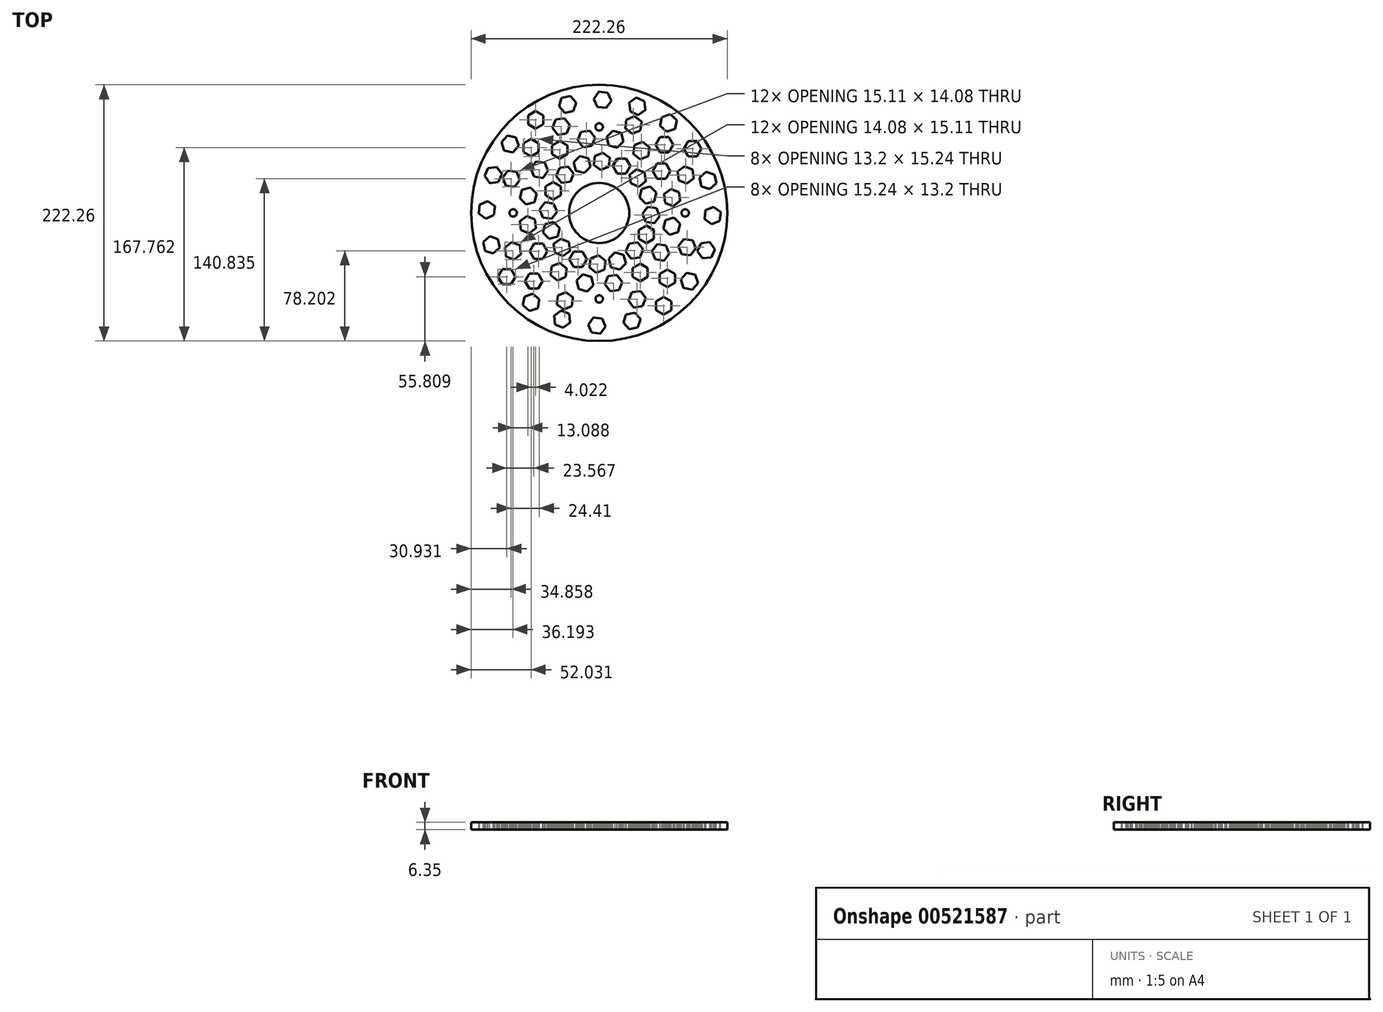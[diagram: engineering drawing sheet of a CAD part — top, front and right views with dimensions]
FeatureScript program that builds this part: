
annotation { "Feature Type Name" : "Feature", "Feature Type Description" : "" }
export const myFeature = defineFeature(function(context is Context, id is Id, definition is map)
    precondition{}
    {
        {
            var Q0;
            Q0=qCreatedBy(makeId("Top.planeOp"),FACE);
            var sketch = newSketch(context, id + "F0", { "sketchPlane" : qUnion([Q0])});
            skCircle(sketch, "E0", {"center": v(0, 0) * mm, "radius": 111.13 * mm});
            skSolve(sketch);
        }
        {
            var Q0;
            Q0=makeQuery(id+"F0.imprint","IMPRINT",FACE,{"disambiguationData":[TD([[makeQuery(id+"F0.imprint","IMPRINT",EDGE,{"derivedFrom":sQuery(id+"F0.wireOp",EDGE,"E0")}),1.0]])]});
            extrude(context, id + "F1", {"entities" : qUnion([Q0]), "depth" : 6.35 * mm, "offsetDistance" : 25.4 * mm});
        }
        {
            var Q0;
            Q0=makeQuery(id+"F1.opExtrude","CAP_FACE",FACE,{"disambiguationData":[OSD([sQuery(id+"F0.wireOp",EDGE,"E0")])],"isStart":false});
            var sketch = newSketch(context, id + "F2", { "sketchPlane" : qUnion([Q0])});
            skCircle(sketch, "E1", {"center": v(0, 0) * mm, "radius": 74.61 * mm, "construction": true});
            skPoint(sketch, "E2", {"position": v(-74.61, 0) * mm});
            skPoint(sketch, "E3", {"position": v(0, -74.61) * mm});
            skPoint(sketch, "E4", {"position": v(74.61, 0) * mm});
            skPoint(sketch, "E5", {"position": v(0, 74.61) * mm});
            skSolve(sketch);
        }
        {
            var Q0;
            Q0=sQuery(id+"F2.wireOp",VERTEX,"E5");
            var Q1;
            Q1=sQuery(id+"F2.wireOp",VERTEX,"E4");
            var Q2;
            Q2=sQuery(id+"F2.wireOp",VERTEX,"E3");
            var Q3;
            Q3=sQuery(id+"F2.wireOp",VERTEX,"E2");
            var Q4;
            Q4=makeQuery(id+"F1.opExtrude","SWEPT_BODY",BODY,{"disambiguationData":[OSD([sQuery(id+"F0.wireOp",EDGE,"E0")])]});
            hole(context, id + "F3", {"style" : HoleStyle.SIMPLE, "endStyle" : HoleEndStyle.THROUGH, "holeDiameter" : 6.35 * mm, "majorDiameter" : 6.35 * mm, "tappedDepth" : 25.4 * mm, "tapClearance" : 3, "locations" : qUnion([Q0, Q1, Q2, Q3]), "scope" : qUnion([Q4])});
        }
        {
            var Q0;
            Q0=makeQuery(id+"F1.opExtrude","CAP_FACE",FACE,{"disambiguationData":[OSD([sQuery(id+"F0.wireOp",EDGE,"E0")])],"isStart":false});
            var sketch = newSketch(context, id + "F4", { "sketchPlane" : qUnion([Q0])});
            skCircle(sketch, "E6.cCircle", {"center": v(-55.08, 80.89) * mm, "radius": 6.6 * mm, "construction": true});
            skLineSegment(sketch, "E6.0", {"start": v(-48.48, 84.7) * mm, "end": v(-48.48, 77.08) * mm});
            skLineSegment(sketch, "E6.1", {"start": v(-48.48, 77.08) * mm, "end": v(-55.08, 73.27) * mm});
            skLineSegment(sketch, "E6.2", {"start": v(-55.08, 73.27) * mm, "end": v(-61.68, 77.08) * mm});
            skLineSegment(sketch, "E6.3", {"start": v(-61.68, 77.08) * mm, "end": v(-61.68, 84.7) * mm});
            skLineSegment(sketch, "E6.4", {"start": v(-61.68, 84.7) * mm, "end": v(-55.08, 88.5) * mm});
            skLineSegment(sketch, "E6.5", {"start": v(-55.08, 88.5) * mm, "end": v(-48.48, 84.7) * mm});
            skPoint(sketch, "E6.0.midPoint", {"position": v(-48.48, 80.89) * mm});
            skCircle(sketch, "E7", {"center": v(0, 0) * mm, "radius": 97.86 * mm, "construction": true});
            skLineSegment(sketch, "E8.1.0", {"start": v(-74.93, 52.53) * mm, "end": v(-82.38, 54.11) * mm});
            skLineSegment(sketch, "E8.1.1", {"start": v(-72.19, 65.44) * mm, "end": v(-69.83, 58.2) * mm});
            skLineSegment(sketch, "E8.1.2", {"start": v(-79.64, 67.02) * mm, "end": v(-72.19, 65.44) * mm});
            skLineSegment(sketch, "E8.1.3", {"start": v(-84.74, 61.36) * mm, "end": v(-79.64, 67.02) * mm});
            skLineSegment(sketch, "E8.1.4", {"start": v(-82.38, 54.11) * mm, "end": v(-84.74, 61.36) * mm});
            skCircle(sketch, "E8.1.5", {"center": v(-77.29, 59.78) * mm, "radius": 6.6 * mm, "construction": true});
            skLineSegment(sketch, "E8.1.6", {"start": v(-69.83, 58.2) * mm, "end": v(-74.93, 52.53) * mm});
            skPoint(sketch, "E8.1.7", {"position": v(-71, 61.82) * mm});
            skLineSegment(sketch, "E8.2.0", {"start": v(-87.4, 26.67) * mm, "end": v(-94.98, 25.87) * mm});
            skLineSegment(sketch, "E8.2.1", {"start": v(-88.78, 39.8) * mm, "end": v(-84.3, 33.63) * mm});
            skLineSegment(sketch, "E8.2.2", {"start": v(-96.36, 39) * mm, "end": v(-88.78, 39.8) * mm});
            skLineSegment(sketch, "E8.2.3", {"start": v(-99.46, 32.04) * mm, "end": v(-96.36, 39) * mm});
            skLineSegment(sketch, "E8.2.4", {"start": v(-94.98, 25.87) * mm, "end": v(-99.46, 32.04) * mm});
            skCircle(sketch, "E8.2.5", {"center": v(-91.88, 32.84) * mm, "radius": 6.6 * mm, "construction": true});
            skLineSegment(sketch, "E8.2.6", {"start": v(-84.3, 33.63) * mm, "end": v(-87.4, 26.67) * mm});
            skPoint(sketch, "E8.2.7", {"position": v(-86.54, 36.71) * mm});
            skLineSegment(sketch, "E8.3.0", {"start": v(-91.28, -1.78) * mm, "end": v(-98.24, -4.88) * mm});
            skLineSegment(sketch, "E8.3.1", {"start": v(-96.64, 10.28) * mm, "end": v(-90.48, 5.8) * mm});
            skLineSegment(sketch, "E8.3.2", {"start": v(-103.6, 7.18) * mm, "end": v(-96.64, 10.28) * mm});
            skLineSegment(sketch, "E8.3.3", {"start": v(-104.4, -0.4) * mm, "end": v(-103.6, 7.18) * mm});
            skLineSegment(sketch, "E8.3.4", {"start": v(-98.24, -4.88) * mm, "end": v(-104.4, -0.4) * mm});
            skCircle(sketch, "E8.3.5", {"center": v(-97.44, 2.7) * mm, "radius": 6.6 * mm, "construction": true});
            skLineSegment(sketch, "E8.3.6", {"start": v(-90.48, 5.8) * mm, "end": v(-91.28, -1.78) * mm});
            skPoint(sketch, "E8.3.7", {"position": v(-93.56, 8.04) * mm});
            skLineSegment(sketch, "E8.4.0", {"start": v(-86.17, -30.03) * mm, "end": v(-91.83, -35.13) * mm});
            skLineSegment(sketch, "E8.4.1", {"start": v(-95, -20.22) * mm, "end": v(-87.75, -22.58) * mm});
            skLineSegment(sketch, "E8.4.2", {"start": v(-100.66, -25.32) * mm, "end": v(-95, -20.22) * mm});
            skLineSegment(sketch, "E8.4.3", {"start": v(-99.08, -32.77) * mm, "end": v(-100.66, -25.32) * mm});
            skLineSegment(sketch, "E8.4.4", {"start": v(-91.83, -35.13) * mm, "end": v(-99.08, -32.77) * mm});
            skCircle(sketch, "E8.4.5", {"center": v(-93.42, -27.68) * mm, "radius": 6.6 * mm, "construction": true});
            skLineSegment(sketch, "E8.4.6", {"start": v(-87.75, -22.58) * mm, "end": v(-86.17, -30.03) * mm});
            skPoint(sketch, "E8.4.7", {"position": v(-91.38, -21.4) * mm});
            skLineSegment(sketch, "E8.5.0", {"start": v(-72.58, -55.32) * mm, "end": v(-76.39, -61.92) * mm});
            skLineSegment(sketch, "E8.5.1", {"start": v(-84, -48.72) * mm, "end": v(-76.39, -48.72) * mm});
            skLineSegment(sketch, "E8.5.2", {"start": v(-87.82, -55.32) * mm, "end": v(-84, -48.72) * mm});
            skLineSegment(sketch, "E8.5.3", {"start": v(-84, -61.92) * mm, "end": v(-87.82, -55.32) * mm});
            skLineSegment(sketch, "E8.5.4", {"start": v(-76.39, -61.92) * mm, "end": v(-84, -61.92) * mm});
            skCircle(sketch, "E8.5.5", {"center": v(-80.2, -55.32) * mm, "radius": 6.6 * mm, "construction": true});
            skLineSegment(sketch, "E8.5.6", {"start": v(-76.39, -48.72) * mm, "end": v(-72.58, -55.32) * mm});
            skPoint(sketch, "E8.5.7", {"position": v(-80.2, -48.72) * mm});
            skLineSegment(sketch, "E8.6.0", {"start": v(-51.84, -75.18) * mm, "end": v(-53.42, -82.63) * mm});
            skLineSegment(sketch, "E8.6.1", {"start": v(-64.75, -72.43) * mm, "end": v(-57.5, -70.08) * mm});
            skLineSegment(sketch, "E8.6.2", {"start": v(-66.33, -79.88) * mm, "end": v(-64.75, -72.43) * mm});
            skLineSegment(sketch, "E8.6.3", {"start": v(-60.67, -84.98) * mm, "end": v(-66.33, -79.88) * mm});
            skLineSegment(sketch, "E8.6.4", {"start": v(-53.42, -82.63) * mm, "end": v(-60.67, -84.98) * mm});
            skCircle(sketch, "E8.6.5", {"center": v(-59.09, -77.53) * mm, "radius": 6.6 * mm, "construction": true});
            skLineSegment(sketch, "E8.6.6", {"start": v(-57.5, -70.08) * mm, "end": v(-51.84, -75.18) * mm});
            skPoint(sketch, "E8.6.7", {"position": v(-61.13, -71.25) * mm});
            skLineSegment(sketch, "E8.7.0", {"start": v(-25.98, -87.65) * mm, "end": v(-25.18, -95.23) * mm});
            skLineSegment(sketch, "E8.7.1", {"start": v(-39.1, -89.03) * mm, "end": v(-32.94, -84.55) * mm});
            skLineSegment(sketch, "E8.7.2", {"start": v(-38.3, -96.6) * mm, "end": v(-39.1, -89.03) * mm});
            skLineSegment(sketch, "E8.7.3", {"start": v(-31.35, -99.7) * mm, "end": v(-38.3, -96.6) * mm});
            skLineSegment(sketch, "E8.7.4", {"start": v(-25.18, -95.23) * mm, "end": v(-31.35, -99.7) * mm});
            skCircle(sketch, "E8.7.5", {"center": v(-32.14, -92.13) * mm, "radius": 6.6 * mm, "construction": true});
            skLineSegment(sketch, "E8.7.6", {"start": v(-32.94, -84.55) * mm, "end": v(-25.98, -87.65) * mm});
            skPoint(sketch, "E8.7.7", {"position": v(-36.02, -86.79) * mm});
            skLineSegment(sketch, "E8.8.0", {"start": v(2.47, -91.52) * mm, "end": v(5.57, -98.48) * mm});
            skLineSegment(sketch, "E8.8.1", {"start": v(-9.59, -96.89) * mm, "end": v(-5.11, -90.72) * mm});
            skLineSegment(sketch, "E8.8.2", {"start": v(-6.49, -103.85) * mm, "end": v(-9.59, -96.89) * mm});
            skLineSegment(sketch, "E8.8.3", {"start": v(1.09, -104.65) * mm, "end": v(-6.49, -103.85) * mm});
            skLineSegment(sketch, "E8.8.4", {"start": v(5.57, -98.48) * mm, "end": v(1.09, -104.65) * mm});
            skCircle(sketch, "E8.8.5", {"center": v(-2.01, -97.69) * mm, "radius": 6.6 * mm, "construction": true});
            skLineSegment(sketch, "E8.8.6", {"start": v(-5.11, -90.72) * mm, "end": v(2.47, -91.52) * mm});
            skPoint(sketch, "E8.8.7", {"position": v(-7.35, -93.8) * mm});
            skLineSegment(sketch, "E8.9.0", {"start": v(30.72, -86.41) * mm, "end": v(35.82, -92.07) * mm});
            skLineSegment(sketch, "E8.9.1", {"start": v(20.91, -95.24) * mm, "end": v(23.27, -88) * mm});
            skLineSegment(sketch, "E8.9.2", {"start": v(26.01, -100.9) * mm, "end": v(20.91, -95.24) * mm});
            skLineSegment(sketch, "E8.9.3", {"start": v(33.46, -99.32) * mm, "end": v(26.01, -100.9) * mm});
            skLineSegment(sketch, "E8.9.4", {"start": v(35.82, -92.07) * mm, "end": v(33.46, -99.32) * mm});
            skCircle(sketch, "E8.9.5", {"center": v(28.37, -93.66) * mm, "radius": 6.6 * mm, "construction": true});
            skLineSegment(sketch, "E8.9.6", {"start": v(23.27, -88) * mm, "end": v(30.72, -86.41) * mm});
            skPoint(sketch, "E8.9.7", {"position": v(22.09, -91.62) * mm});
            skLineSegment(sketch, "E8.10.0", {"start": v(56.01, -72.82) * mm, "end": v(62.61, -76.63) * mm});
            skLineSegment(sketch, "E8.10.1", {"start": v(49.41, -84.25) * mm, "end": v(49.41, -76.63) * mm});
            skLineSegment(sketch, "E8.10.2", {"start": v(56.01, -88.06) * mm, "end": v(49.41, -84.25) * mm});
            skLineSegment(sketch, "E8.10.3", {"start": v(62.61, -84.25) * mm, "end": v(56.01, -88.06) * mm});
            skLineSegment(sketch, "E8.10.4", {"start": v(62.61, -76.63) * mm, "end": v(62.61, -84.25) * mm});
            skCircle(sketch, "E8.10.5", {"center": v(56.01, -80.44) * mm, "radius": 6.6 * mm, "construction": true});
            skLineSegment(sketch, "E8.10.6", {"start": v(49.41, -76.63) * mm, "end": v(56.01, -72.82) * mm});
            skPoint(sketch, "E8.10.7", {"position": v(49.41, -80.44) * mm});
            skLineSegment(sketch, "E8.11.0", {"start": v(75.87, -52.08) * mm, "end": v(83.32, -53.67) * mm});
            skLineSegment(sketch, "E8.11.1", {"start": v(73.12, -65) * mm, "end": v(70.77, -57.75) * mm});
            skLineSegment(sketch, "E8.11.2", {"start": v(80.58, -66.58) * mm, "end": v(73.12, -65) * mm});
            skLineSegment(sketch, "E8.11.3", {"start": v(85.67, -60.91) * mm, "end": v(80.58, -66.58) * mm});
            skLineSegment(sketch, "E8.11.4", {"start": v(83.32, -53.67) * mm, "end": v(85.67, -60.91) * mm});
            skCircle(sketch, "E8.11.5", {"center": v(78.22, -59.33) * mm, "radius": 6.6 * mm, "construction": true});
            skLineSegment(sketch, "E8.11.6", {"start": v(70.77, -57.75) * mm, "end": v(75.87, -52.08) * mm});
            skPoint(sketch, "E8.11.7", {"position": v(71.94, -61.37) * mm});
            skLineSegment(sketch, "E8.12.0", {"start": v(88.34, -26.22) * mm, "end": v(95.92, -25.43) * mm});
            skLineSegment(sketch, "E8.12.1", {"start": v(89.72, -39.35) * mm, "end": v(85.24, -33.19) * mm});
            skLineSegment(sketch, "E8.12.2", {"start": v(97.3, -38.55) * mm, "end": v(89.72, -39.35) * mm});
            skLineSegment(sketch, "E8.12.3", {"start": v(100.4, -31.6) * mm, "end": v(97.3, -38.55) * mm});
            skLineSegment(sketch, "E8.12.4", {"start": v(95.92, -25.43) * mm, "end": v(100.4, -31.6) * mm});
            skCircle(sketch, "E8.12.5", {"center": v(92.82, -32.39) * mm, "radius": 6.6 * mm, "construction": true});
            skLineSegment(sketch, "E8.12.6", {"start": v(85.24, -33.19) * mm, "end": v(88.34, -26.22) * mm});
            skPoint(sketch, "E8.12.7", {"position": v(87.48, -36.27) * mm});
            skLineSegment(sketch, "E8.13.0", {"start": v(92.21, 2.22) * mm, "end": v(99.17, 5.32) * mm});
            skLineSegment(sketch, "E8.13.1", {"start": v(97.58, -9.83) * mm, "end": v(91.41, -5.35) * mm});
            skLineSegment(sketch, "E8.13.2", {"start": v(104.54, -6.73) * mm, "end": v(97.58, -9.83) * mm});
            skLineSegment(sketch, "E8.13.3", {"start": v(105.34, 0.84) * mm, "end": v(104.54, -6.73) * mm});
            skLineSegment(sketch, "E8.13.4", {"start": v(99.17, 5.32) * mm, "end": v(105.34, 0.84) * mm});
            skCircle(sketch, "E8.13.5", {"center": v(98.38, -2.25) * mm, "radius": 6.6 * mm, "construction": true});
            skLineSegment(sketch, "E8.13.6", {"start": v(91.41, -5.35) * mm, "end": v(92.21, 2.22) * mm});
            skPoint(sketch, "E8.13.7", {"position": v(94.5, -7.6) * mm});
            skLineSegment(sketch, "E8.14.0", {"start": v(87.1, 30.48) * mm, "end": v(92.77, 35.58) * mm});
            skLineSegment(sketch, "E8.14.1", {"start": v(95.93, 20.67) * mm, "end": v(88.69, 23.02) * mm});
            skLineSegment(sketch, "E8.14.2", {"start": v(101.6, 25.77) * mm, "end": v(95.93, 20.67) * mm});
            skLineSegment(sketch, "E8.14.3", {"start": v(100.01, 33.22) * mm, "end": v(101.6, 25.77) * mm});
            skLineSegment(sketch, "E8.14.4", {"start": v(92.77, 35.58) * mm, "end": v(100.01, 33.22) * mm});
            skCircle(sketch, "E8.14.5", {"center": v(94.35, 28.12) * mm, "radius": 6.6 * mm, "construction": true});
            skLineSegment(sketch, "E8.14.6", {"start": v(88.69, 23.02) * mm, "end": v(87.1, 30.48) * mm});
            skPoint(sketch, "E8.14.7", {"position": v(92.31, 21.85) * mm});
            skLineSegment(sketch, "E8.15.0", {"start": v(73.51, 55.77) * mm, "end": v(77.32, 62.37) * mm});
            skLineSegment(sketch, "E8.15.1", {"start": v(84.94, 49.17) * mm, "end": v(77.32, 49.17) * mm});
            skLineSegment(sketch, "E8.15.2", {"start": v(88.75, 55.77) * mm, "end": v(84.94, 49.17) * mm});
            skLineSegment(sketch, "E8.15.3", {"start": v(84.94, 62.37) * mm, "end": v(88.75, 55.77) * mm});
            skLineSegment(sketch, "E8.15.4", {"start": v(77.32, 62.37) * mm, "end": v(84.94, 62.37) * mm});
            skCircle(sketch, "E8.15.5", {"center": v(81.13, 55.77) * mm, "radius": 6.6 * mm, "construction": true});
            skLineSegment(sketch, "E8.15.6", {"start": v(77.32, 49.17) * mm, "end": v(73.51, 55.77) * mm});
            skPoint(sketch, "E8.15.7", {"position": v(81.13, 49.17) * mm});
            skPoint(sketch, "E8.center", {"position": v(0.47, 0.22) * mm});
            skCircle(sketch, "E9.cCircle", {"center": v(-59.1, 56.63) * mm, "radius": 6.6 * mm, "construction": true});
            skLineSegment(sketch, "E9.0", {"start": v(-52.5, 60.44) * mm, "end": v(-52.5, 52.82) * mm});
            skLineSegment(sketch, "E9.1", {"start": v(-52.5, 52.82) * mm, "end": v(-59.1, 49.01) * mm});
            skLineSegment(sketch, "E9.2", {"start": v(-59.1, 49.01) * mm, "end": v(-65.7, 52.82) * mm});
            skLineSegment(sketch, "E9.3", {"start": v(-65.7, 52.82) * mm, "end": v(-65.7, 60.44) * mm});
            skLineSegment(sketch, "E9.4", {"start": v(-65.7, 60.44) * mm, "end": v(-59.1, 64.25) * mm});
            skLineSegment(sketch, "E9.5", {"start": v(-59.1, 64.25) * mm, "end": v(-52.5, 60.44) * mm});
            skPoint(sketch, "E9.0.midPoint", {"position": v(-52.5, 56.63) * mm});
            skLineSegment(sketch, "E10.1.0", {"start": v(-73.36, 22.66) * mm, "end": v(-80.91, 23.66) * mm});
            skLineSegment(sketch, "E10.1.1", {"start": v(-71.63, 35.75) * mm, "end": v(-68.72, 28.71) * mm});
            skLineSegment(sketch, "E10.1.2", {"start": v(-79.19, 36.74) * mm, "end": v(-71.63, 35.75) * mm});
            skLineSegment(sketch, "E10.1.3", {"start": v(-83.83, 30.7) * mm, "end": v(-79.19, 36.74) * mm});
            skLineSegment(sketch, "E10.1.4", {"start": v(-80.91, 23.66) * mm, "end": v(-83.83, 30.7) * mm});
            skCircle(sketch, "E10.1.5", {"center": v(-76.27, 29.7) * mm, "radius": 6.6 * mm, "construction": true});
            skLineSegment(sketch, "E10.1.6", {"start": v(-68.72, 28.71) * mm, "end": v(-73.36, 22.66) * mm});
            skPoint(sketch, "E10.1.7", {"position": v(-70.18, 32.23) * mm});
            skLineSegment(sketch, "E10.3.0", {"start": v(-67.9, -35.84) * mm, "end": v(-73.94, -40.48) * mm});
            skLineSegment(sketch, "E10.3.1", {"start": v(-75.93, -25.37) * mm, "end": v(-68.9, -28.29) * mm});
            skLineSegment(sketch, "E10.3.2", {"start": v(-81.98, -30.01) * mm, "end": v(-75.93, -25.37) * mm});
            skLineSegment(sketch, "E10.3.3", {"start": v(-80.98, -37.57) * mm, "end": v(-81.98, -30.01) * mm});
            skLineSegment(sketch, "E10.3.4", {"start": v(-73.94, -40.48) * mm, "end": v(-80.98, -37.57) * mm});
            skCircle(sketch, "E10.3.5", {"center": v(-74.94, -32.93) * mm, "radius": 6.6 * mm, "construction": true});
            skLineSegment(sketch, "E10.3.6", {"start": v(-68.9, -28.29) * mm, "end": v(-67.9, -35.84) * mm});
            skPoint(sketch, "E10.3.7", {"position": v(-72.41, -26.83) * mm});
            skLineSegment(sketch, "E10.4.0", {"start": v(-49.01, -59.1) * mm, "end": v(-52.82, -65.7) * mm});
            skLineSegment(sketch, "E10.4.1", {"start": v(-60.44, -52.5) * mm, "end": v(-52.82, -52.5) * mm});
            skLineSegment(sketch, "E10.4.2", {"start": v(-64.25, -59.1) * mm, "end": v(-60.44, -52.5) * mm});
            skLineSegment(sketch, "E10.4.3", {"start": v(-60.44, -65.7) * mm, "end": v(-64.25, -59.1) * mm});
            skLineSegment(sketch, "E10.4.4", {"start": v(-52.82, -65.7) * mm, "end": v(-60.44, -65.7) * mm});
            skCircle(sketch, "E10.4.5", {"center": v(-56.63, -59.1) * mm, "radius": 6.6 * mm, "construction": true});
            skLineSegment(sketch, "E10.4.6", {"start": v(-52.82, -52.5) * mm, "end": v(-49.01, -59.1) * mm});
            skPoint(sketch, "E10.4.7", {"position": v(-56.63, -52.5) * mm});
            skLineSegment(sketch, "E10.5.0", {"start": v(-22.66, -73.36) * mm, "end": v(-23.66, -80.91) * mm});
            skLineSegment(sketch, "E10.5.1", {"start": v(-35.75, -71.63) * mm, "end": v(-28.71, -68.72) * mm});
            skLineSegment(sketch, "E10.5.2", {"start": v(-36.74, -79.19) * mm, "end": v(-35.75, -71.63) * mm});
            skLineSegment(sketch, "E10.5.3", {"start": v(-30.7, -83.83) * mm, "end": v(-36.74, -79.19) * mm});
            skLineSegment(sketch, "E10.5.4", {"start": v(-23.66, -80.91) * mm, "end": v(-30.7, -83.83) * mm});
            skCircle(sketch, "E10.5.5", {"center": v(-29.7, -76.27) * mm, "radius": 6.6 * mm, "construction": true});
            skLineSegment(sketch, "E10.5.6", {"start": v(-28.71, -68.72) * mm, "end": v(-22.66, -73.36) * mm});
            skPoint(sketch, "E10.5.7", {"position": v(-32.23, -70.18) * mm});
            skLineSegment(sketch, "E10.7.0", {"start": v(35.84, -67.9) * mm, "end": v(40.48, -73.94) * mm});
            skLineSegment(sketch, "E10.7.1", {"start": v(25.37, -75.93) * mm, "end": v(28.29, -68.9) * mm});
            skLineSegment(sketch, "E10.7.2", {"start": v(30.01, -81.98) * mm, "end": v(25.37, -75.93) * mm});
            skLineSegment(sketch, "E10.7.3", {"start": v(37.57, -80.98) * mm, "end": v(30.01, -81.98) * mm});
            skLineSegment(sketch, "E10.7.4", {"start": v(40.48, -73.94) * mm, "end": v(37.57, -80.98) * mm});
            skCircle(sketch, "E10.7.5", {"center": v(32.93, -74.94) * mm, "radius": 6.6 * mm, "construction": true});
            skLineSegment(sketch, "E10.7.6", {"start": v(28.29, -68.9) * mm, "end": v(35.84, -67.9) * mm});
            skPoint(sketch, "E10.7.7", {"position": v(26.83, -72.41) * mm});
            skLineSegment(sketch, "E10.8.0", {"start": v(59.1, -49.01) * mm, "end": v(65.7, -52.82) * mm});
            skLineSegment(sketch, "E10.8.1", {"start": v(52.5, -60.44) * mm, "end": v(52.5, -52.82) * mm});
            skLineSegment(sketch, "E10.8.2", {"start": v(59.1, -64.25) * mm, "end": v(52.5, -60.44) * mm});
            skLineSegment(sketch, "E10.8.3", {"start": v(65.7, -60.44) * mm, "end": v(59.1, -64.25) * mm});
            skLineSegment(sketch, "E10.8.4", {"start": v(65.7, -52.82) * mm, "end": v(65.7, -60.44) * mm});
            skCircle(sketch, "E10.8.5", {"center": v(59.1, -56.63) * mm, "radius": 6.6 * mm, "construction": true});
            skLineSegment(sketch, "E10.8.6", {"start": v(52.5, -52.82) * mm, "end": v(59.1, -49.01) * mm});
            skPoint(sketch, "E10.8.7", {"position": v(52.5, -56.63) * mm});
            skLineSegment(sketch, "E10.9.0", {"start": v(73.36, -22.66) * mm, "end": v(80.91, -23.66) * mm});
            skLineSegment(sketch, "E10.9.1", {"start": v(71.63, -35.75) * mm, "end": v(68.72, -28.71) * mm});
            skLineSegment(sketch, "E10.9.2", {"start": v(79.19, -36.74) * mm, "end": v(71.63, -35.75) * mm});
            skLineSegment(sketch, "E10.9.3", {"start": v(83.83, -30.7) * mm, "end": v(79.19, -36.74) * mm});
            skLineSegment(sketch, "E10.9.4", {"start": v(80.91, -23.66) * mm, "end": v(83.83, -30.7) * mm});
            skCircle(sketch, "E10.9.5", {"center": v(76.27, -29.7) * mm, "radius": 6.6 * mm, "construction": true});
            skLineSegment(sketch, "E10.9.6", {"start": v(68.72, -28.71) * mm, "end": v(73.36, -22.66) * mm});
            skPoint(sketch, "E10.9.7", {"position": v(70.18, -32.23) * mm});
            skLineSegment(sketch, "E10.11.0", {"start": v(67.9, 35.84) * mm, "end": v(73.94, 40.48) * mm});
            skLineSegment(sketch, "E10.11.1", {"start": v(75.93, 25.37) * mm, "end": v(68.9, 28.29) * mm});
            skLineSegment(sketch, "E10.11.2", {"start": v(81.98, 30.01) * mm, "end": v(75.93, 25.37) * mm});
            skLineSegment(sketch, "E10.11.3", {"start": v(80.98, 37.57) * mm, "end": v(81.98, 30.01) * mm});
            skLineSegment(sketch, "E10.11.4", {"start": v(73.94, 40.48) * mm, "end": v(80.98, 37.57) * mm});
            skCircle(sketch, "E10.11.5", {"center": v(74.94, 32.93) * mm, "radius": 6.6 * mm, "construction": true});
            skLineSegment(sketch, "E10.11.6", {"start": v(68.9, 28.29) * mm, "end": v(67.9, 35.84) * mm});
            skPoint(sketch, "E10.11.7", {"position": v(72.41, 26.83) * mm});
            skLineSegment(sketch, "E10.12.0", {"start": v(49.01, 59.1) * mm, "end": v(52.82, 65.7) * mm});
            skLineSegment(sketch, "E10.12.1", {"start": v(60.44, 52.5) * mm, "end": v(52.82, 52.5) * mm});
            skLineSegment(sketch, "E10.12.2", {"start": v(64.25, 59.1) * mm, "end": v(60.44, 52.5) * mm});
            skLineSegment(sketch, "E10.12.3", {"start": v(60.44, 65.7) * mm, "end": v(64.25, 59.1) * mm});
            skLineSegment(sketch, "E10.12.4", {"start": v(52.82, 65.7) * mm, "end": v(60.44, 65.7) * mm});
            skCircle(sketch, "E10.12.5", {"center": v(56.63, 59.1) * mm, "radius": 6.6 * mm, "construction": true});
            skLineSegment(sketch, "E10.12.6", {"start": v(52.82, 52.5) * mm, "end": v(49.01, 59.1) * mm});
            skPoint(sketch, "E10.12.7", {"position": v(56.63, 52.5) * mm});
            skLineSegment(sketch, "E10.13.0", {"start": v(22.66, 73.36) * mm, "end": v(23.66, 80.91) * mm});
            skLineSegment(sketch, "E10.13.1", {"start": v(35.75, 71.63) * mm, "end": v(28.71, 68.72) * mm});
            skLineSegment(sketch, "E10.13.2", {"start": v(36.74, 79.19) * mm, "end": v(35.75, 71.63) * mm});
            skLineSegment(sketch, "E10.13.3", {"start": v(30.7, 83.83) * mm, "end": v(36.74, 79.19) * mm});
            skLineSegment(sketch, "E10.13.4", {"start": v(23.66, 80.91) * mm, "end": v(30.7, 83.83) * mm});
            skCircle(sketch, "E10.13.5", {"center": v(29.7, 76.27) * mm, "radius": 6.6 * mm, "construction": true});
            skLineSegment(sketch, "E10.13.6", {"start": v(28.71, 68.72) * mm, "end": v(22.66, 73.36) * mm});
            skPoint(sketch, "E10.13.7", {"position": v(32.23, 70.18) * mm});
            skLineSegment(sketch, "E10.15.0", {"start": v(-35.84, 67.9) * mm, "end": v(-40.48, 73.94) * mm});
            skLineSegment(sketch, "E10.15.1", {"start": v(-25.37, 75.93) * mm, "end": v(-28.29, 68.9) * mm});
            skLineSegment(sketch, "E10.15.2", {"start": v(-30.01, 81.98) * mm, "end": v(-25.37, 75.93) * mm});
            skLineSegment(sketch, "E10.15.3", {"start": v(-37.57, 80.98) * mm, "end": v(-30.01, 81.98) * mm});
            skLineSegment(sketch, "E10.15.4", {"start": v(-40.48, 73.94) * mm, "end": v(-37.57, 80.98) * mm});
            skCircle(sketch, "E10.15.5", {"center": v(-32.93, 74.94) * mm, "radius": 6.6 * mm, "construction": true});
            skLineSegment(sketch, "E10.15.6", {"start": v(-28.29, 68.9) * mm, "end": v(-35.84, 67.9) * mm});
            skPoint(sketch, "E10.15.7", {"position": v(-26.83, 72.41) * mm});
            skCircle(sketch, "E11.cCircle", {"center": v(-34.13, 54.85) * mm, "radius": 6.6 * mm, "construction": true});
            skLineSegment(sketch, "E11.0", {"start": v(-27.53, 58.66) * mm, "end": v(-27.53, 51.04) * mm});
            skLineSegment(sketch, "E11.1", {"start": v(-27.53, 51.04) * mm, "end": v(-34.13, 47.23) * mm});
            skLineSegment(sketch, "E11.2", {"start": v(-34.13, 47.23) * mm, "end": v(-40.73, 51.04) * mm});
            skLineSegment(sketch, "E11.3", {"start": v(-40.73, 51.04) * mm, "end": v(-40.73, 58.66) * mm});
            skLineSegment(sketch, "E11.4", {"start": v(-40.73, 58.66) * mm, "end": v(-34.13, 62.47) * mm});
            skLineSegment(sketch, "E11.5", {"start": v(-34.13, 62.47) * mm, "end": v(-27.53, 58.66) * mm});
            skPoint(sketch, "E11.0.midPoint", {"position": v(-27.53, 54.85) * mm});
            skCircle(sketch, "E12", {"center": v(0, 0) * mm, "radius": 64.6 * mm, "construction": true});
            skLineSegment(sketch, "E13.1.0", {"start": v(-48.95, 30.44) * mm, "end": v(-56.5, 31.43) * mm});
            skLineSegment(sketch, "E13.1.1", {"start": v(-47.22, 43.52) * mm, "end": v(-44.3, 36.48) * mm});
            skLineSegment(sketch, "E13.1.2", {"start": v(-54.78, 44.52) * mm, "end": v(-47.22, 43.52) * mm});
            skLineSegment(sketch, "E13.1.3", {"start": v(-59.42, 38.47) * mm, "end": v(-54.78, 44.52) * mm});
            skLineSegment(sketch, "E13.1.4", {"start": v(-56.5, 31.43) * mm, "end": v(-59.42, 38.47) * mm});
            skCircle(sketch, "E13.1.5", {"center": v(-51.86, 37.48) * mm, "radius": 6.6 * mm, "construction": true});
            skLineSegment(sketch, "E13.1.6", {"start": v(-44.3, 36.48) * mm, "end": v(-48.95, 30.44) * mm});
            skPoint(sketch, "E13.1.7", {"position": v(-45.77, 40) * mm});
            skLineSegment(sketch, "E13.2.0", {"start": v(-56.2, 9.25) * mm, "end": v(-63.57, 7.28) * mm});
            skLineSegment(sketch, "E13.2.1", {"start": v(-59.62, 22) * mm, "end": v(-54.24, 16.61) * mm});
            skLineSegment(sketch, "E13.2.2", {"start": v(-66.98, 20.03) * mm, "end": v(-59.62, 22) * mm});
            skLineSegment(sketch, "E13.2.3", {"start": v(-68.96, 12.67) * mm, "end": v(-66.98, 20.03) * mm});
            skLineSegment(sketch, "E13.2.4", {"start": v(-63.57, 7.28) * mm, "end": v(-68.96, 12.67) * mm});
            skCircle(sketch, "E13.2.5", {"center": v(-61.6, 14.64) * mm, "radius": 6.6 * mm, "construction": true});
            skLineSegment(sketch, "E13.2.6", {"start": v(-54.24, 16.61) * mm, "end": v(-56.2, 9.25) * mm});
            skPoint(sketch, "E13.2.7", {"position": v(-56.93, 19.3) * mm});
            skLineSegment(sketch, "E13.3.0", {"start": v(-54.8, -13.1) * mm, "end": v(-60.85, -17.74) * mm});
            skLineSegment(sketch, "E13.3.1", {"start": v(-62.84, -2.63) * mm, "end": v(-55.8, -5.55) * mm});
            skLineSegment(sketch, "E13.3.2", {"start": v(-68.89, -7.27) * mm, "end": v(-62.84, -2.63) * mm});
            skLineSegment(sketch, "E13.3.3", {"start": v(-67.9, -14.82) * mm, "end": v(-68.89, -7.27) * mm});
            skLineSegment(sketch, "E13.3.4", {"start": v(-60.85, -17.74) * mm, "end": v(-67.9, -14.82) * mm});
            skCircle(sketch, "E13.3.5", {"center": v(-61.85, -10.19) * mm, "radius": 6.6 * mm, "construction": true});
            skLineSegment(sketch, "E13.3.6", {"start": v(-55.8, -5.55) * mm, "end": v(-54.8, -13.1) * mm});
            skPoint(sketch, "E13.3.7", {"position": v(-59.32, -4.09) * mm});
            skLineSegment(sketch, "E13.4.0", {"start": v(-44.96, -33.22) * mm, "end": v(-48.77, -39.82) * mm});
            skLineSegment(sketch, "E13.4.1", {"start": v(-56.4, -26.62) * mm, "end": v(-48.77, -26.62) * mm});
            skLineSegment(sketch, "E13.4.2", {"start": v(-60.2, -33.22) * mm, "end": v(-56.4, -26.62) * mm});
            skLineSegment(sketch, "E13.4.3", {"start": v(-56.4, -39.82) * mm, "end": v(-60.2, -33.22) * mm});
            skLineSegment(sketch, "E13.4.4", {"start": v(-48.77, -39.82) * mm, "end": v(-56.4, -39.82) * mm});
            skCircle(sketch, "E13.4.5", {"center": v(-52.58, -33.22) * mm, "radius": 6.6 * mm, "construction": true});
            skLineSegment(sketch, "E13.4.6", {"start": v(-48.77, -26.62) * mm, "end": v(-44.96, -33.22) * mm});
            skPoint(sketch, "E13.4.7", {"position": v(-52.58, -26.62) * mm});
            skLineSegment(sketch, "E13.5.0", {"start": v(-28.17, -48.03) * mm, "end": v(-29.16, -55.59) * mm});
            skLineSegment(sketch, "E13.5.1", {"start": v(-41.25, -46.31) * mm, "end": v(-34.21, -43.4) * mm});
            skLineSegment(sketch, "E13.5.2", {"start": v(-42.25, -53.87) * mm, "end": v(-41.25, -46.31) * mm});
            skLineSegment(sketch, "E13.5.3", {"start": v(-36.2, -58.5) * mm, "end": v(-42.25, -53.87) * mm});
            skLineSegment(sketch, "E13.5.4", {"start": v(-29.16, -55.59) * mm, "end": v(-36.2, -58.5) * mm});
            skCircle(sketch, "E13.5.5", {"center": v(-35.2, -50.95) * mm, "radius": 6.6 * mm, "construction": true});
            skLineSegment(sketch, "E13.5.6", {"start": v(-34.21, -43.4) * mm, "end": v(-28.17, -48.03) * mm});
            skPoint(sketch, "E13.5.7", {"position": v(-37.73, -44.85) * mm});
            skLineSegment(sketch, "E13.6.0", {"start": v(-6.98, -55.3) * mm, "end": v(-5.01, -62.66) * mm});
            skLineSegment(sketch, "E13.6.1", {"start": v(-19.73, -58.71) * mm, "end": v(-14.34, -53.32) * mm});
            skLineSegment(sketch, "E13.6.2", {"start": v(-17.76, -66.07) * mm, "end": v(-19.73, -58.71) * mm});
            skLineSegment(sketch, "E13.6.3", {"start": v(-10.4, -68.04) * mm, "end": v(-17.76, -66.07) * mm});
            skLineSegment(sketch, "E13.6.4", {"start": v(-5.01, -62.66) * mm, "end": v(-10.4, -68.04) * mm});
            skCircle(sketch, "E13.6.5", {"center": v(-12.37, -60.68) * mm, "radius": 6.6 * mm, "construction": true});
            skLineSegment(sketch, "E13.6.6", {"start": v(-14.34, -53.32) * mm, "end": v(-6.98, -55.3) * mm});
            skPoint(sketch, "E13.6.7", {"position": v(-17.04, -56.02) * mm});
            skLineSegment(sketch, "E13.7.0", {"start": v(15.37, -53.9) * mm, "end": v(20, -59.94) * mm});
            skLineSegment(sketch, "E13.7.1", {"start": v(4.9, -61.93) * mm, "end": v(7.81, -54.9) * mm});
            skLineSegment(sketch, "E13.7.2", {"start": v(9.54, -67.98) * mm, "end": v(4.9, -61.93) * mm});
            skLineSegment(sketch, "E13.7.3", {"start": v(17.1, -66.98) * mm, "end": v(9.54, -67.98) * mm});
            skLineSegment(sketch, "E13.7.4", {"start": v(20, -59.94) * mm, "end": v(17.1, -66.98) * mm});
            skCircle(sketch, "E13.7.5", {"center": v(12.45, -60.94) * mm, "radius": 6.6 * mm, "construction": true});
            skLineSegment(sketch, "E13.7.6", {"start": v(7.81, -54.9) * mm, "end": v(15.37, -53.9) * mm});
            skPoint(sketch, "E13.7.7", {"position": v(6.36, -58.41) * mm});
            skLineSegment(sketch, "E13.8.0", {"start": v(35.48, -44.05) * mm, "end": v(42.08, -47.86) * mm});
            skLineSegment(sketch, "E13.8.1", {"start": v(28.89, -55.48) * mm, "end": v(28.89, -47.86) * mm});
            skLineSegment(sketch, "E13.8.2", {"start": v(35.48, -59.3) * mm, "end": v(28.89, -55.48) * mm});
            skLineSegment(sketch, "E13.8.3", {"start": v(42.08, -55.48) * mm, "end": v(35.48, -59.3) * mm});
            skLineSegment(sketch, "E13.8.4", {"start": v(42.08, -47.86) * mm, "end": v(42.08, -55.48) * mm});
            skCircle(sketch, "E13.8.5", {"center": v(35.48, -51.67) * mm, "radius": 6.6 * mm, "construction": true});
            skLineSegment(sketch, "E13.8.6", {"start": v(28.89, -47.86) * mm, "end": v(35.48, -44.05) * mm});
            skPoint(sketch, "E13.8.7", {"position": v(28.89, -51.67) * mm});
            skLineSegment(sketch, "E13.9.0", {"start": v(50.3, -27.26) * mm, "end": v(57.86, -28.25) * mm});
            skLineSegment(sketch, "E13.9.1", {"start": v(48.58, -40.34) * mm, "end": v(45.66, -33.3) * mm});
            skLineSegment(sketch, "E13.9.2", {"start": v(56.13, -41.34) * mm, "end": v(48.58, -40.34) * mm});
            skLineSegment(sketch, "E13.9.3", {"start": v(60.77, -35.3) * mm, "end": v(56.13, -41.34) * mm});
            skLineSegment(sketch, "E13.9.4", {"start": v(57.86, -28.25) * mm, "end": v(60.77, -35.3) * mm});
            skCircle(sketch, "E13.9.5", {"center": v(53.22, -34.3) * mm, "radius": 6.6 * mm, "construction": true});
            skLineSegment(sketch, "E13.9.6", {"start": v(45.66, -33.3) * mm, "end": v(50.3, -27.26) * mm});
            skPoint(sketch, "E13.9.7", {"position": v(47.12, -36.82) * mm});
            skLineSegment(sketch, "E13.10.0", {"start": v(57.56, -6.07) * mm, "end": v(64.92, -4.1) * mm});
            skLineSegment(sketch, "E13.10.1", {"start": v(60.98, -18.82) * mm, "end": v(55.6, -13.43) * mm});
            skLineSegment(sketch, "E13.10.2", {"start": v(68.34, -16.85) * mm, "end": v(60.98, -18.82) * mm});
            skLineSegment(sketch, "E13.10.3", {"start": v(70.31, -9.49) * mm, "end": v(68.34, -16.85) * mm});
            skLineSegment(sketch, "E13.10.4", {"start": v(64.92, -4.1) * mm, "end": v(70.31, -9.49) * mm});
            skCircle(sketch, "E13.10.5", {"center": v(62.95, -11.46) * mm, "radius": 6.6 * mm, "construction": true});
            skLineSegment(sketch, "E13.10.6", {"start": v(55.6, -13.43) * mm, "end": v(57.56, -6.07) * mm});
            skPoint(sketch, "E13.10.7", {"position": v(58.28, -16.12) * mm});
            skLineSegment(sketch, "E13.11.0", {"start": v(56.16, 16.28) * mm, "end": v(62.2, 20.92) * mm});
            skLineSegment(sketch, "E13.11.1", {"start": v(64.2, 5.81) * mm, "end": v(57.16, 8.73) * mm});
            skLineSegment(sketch, "E13.11.2", {"start": v(70.24, 10.45) * mm, "end": v(64.2, 5.81) * mm});
            skLineSegment(sketch, "E13.11.3", {"start": v(69.25, 18) * mm, "end": v(70.24, 10.45) * mm});
            skLineSegment(sketch, "E13.11.4", {"start": v(62.2, 20.92) * mm, "end": v(69.25, 18) * mm});
            skCircle(sketch, "E13.11.5", {"center": v(63.2, 13.37) * mm, "radius": 6.6 * mm, "construction": true});
            skLineSegment(sketch, "E13.11.6", {"start": v(57.16, 8.73) * mm, "end": v(56.16, 16.28) * mm});
            skPoint(sketch, "E13.11.7", {"position": v(60.68, 7.27) * mm});
            skLineSegment(sketch, "E13.12.0", {"start": v(46.32, 36.4) * mm, "end": v(50.13, 43) * mm});
            skLineSegment(sketch, "E13.12.1", {"start": v(57.75, 29.8) * mm, "end": v(50.13, 29.8) * mm});
            skLineSegment(sketch, "E13.12.2", {"start": v(61.56, 36.4) * mm, "end": v(57.75, 29.8) * mm});
            skLineSegment(sketch, "E13.12.3", {"start": v(57.75, 43) * mm, "end": v(61.56, 36.4) * mm});
            skLineSegment(sketch, "E13.12.4", {"start": v(50.13, 43) * mm, "end": v(57.75, 43) * mm});
            skCircle(sketch, "E13.12.5", {"center": v(53.94, 36.4) * mm, "radius": 6.6 * mm, "construction": true});
            skLineSegment(sketch, "E13.12.6", {"start": v(50.13, 29.8) * mm, "end": v(46.32, 36.4) * mm});
            skPoint(sketch, "E13.12.7", {"position": v(53.94, 29.8) * mm});
            skLineSegment(sketch, "E13.13.0", {"start": v(29.52, 51.21) * mm, "end": v(30.52, 58.77) * mm});
            skLineSegment(sketch, "E13.13.1", {"start": v(42.6, 49.5) * mm, "end": v(35.57, 46.57) * mm});
            skLineSegment(sketch, "E13.13.2", {"start": v(43.6, 57.05) * mm, "end": v(42.6, 49.5) * mm});
            skLineSegment(sketch, "E13.13.3", {"start": v(37.56, 61.68) * mm, "end": v(43.6, 57.05) * mm});
            skLineSegment(sketch, "E13.13.4", {"start": v(30.52, 58.77) * mm, "end": v(37.56, 61.68) * mm});
            skCircle(sketch, "E13.13.5", {"center": v(36.56, 54.13) * mm, "radius": 6.6 * mm, "construction": true});
            skLineSegment(sketch, "E13.13.6", {"start": v(35.57, 46.57) * mm, "end": v(29.52, 51.21) * mm});
            skPoint(sketch, "E13.13.7", {"position": v(39.09, 48.03) * mm});
            skLineSegment(sketch, "E13.14.0", {"start": v(8.34, 58.48) * mm, "end": v(6.37, 65.84) * mm});
            skLineSegment(sketch, "E13.14.1", {"start": v(21.09, 61.9) * mm, "end": v(15.7, 56.5) * mm});
            skLineSegment(sketch, "E13.14.2", {"start": v(19.11, 69.25) * mm, "end": v(21.09, 61.9) * mm});
            skLineSegment(sketch, "E13.14.3", {"start": v(11.75, 71.22) * mm, "end": v(19.11, 69.25) * mm});
            skLineSegment(sketch, "E13.14.4", {"start": v(6.37, 65.84) * mm, "end": v(11.75, 71.22) * mm});
            skCircle(sketch, "E13.14.5", {"center": v(13.73, 63.86) * mm, "radius": 6.6 * mm, "construction": true});
            skLineSegment(sketch, "E13.14.6", {"start": v(15.7, 56.5) * mm, "end": v(8.34, 58.48) * mm});
            skPoint(sketch, "E13.14.7", {"position": v(18.4, 59.2) * mm});
            skLineSegment(sketch, "E13.15.0", {"start": v(-14.01, 57.08) * mm, "end": v(-18.65, 63.12) * mm});
            skLineSegment(sketch, "E13.15.1", {"start": v(-3.54, 65.11) * mm, "end": v(-6.46, 58.07) * mm});
            skLineSegment(sketch, "E13.15.2", {"start": v(-8.18, 71.16) * mm, "end": v(-3.54, 65.11) * mm});
            skLineSegment(sketch, "E13.15.3", {"start": v(-15.74, 70.16) * mm, "end": v(-8.18, 71.16) * mm});
            skLineSegment(sketch, "E13.15.4", {"start": v(-18.65, 63.12) * mm, "end": v(-15.74, 70.16) * mm});
            skCircle(sketch, "E13.15.5", {"center": v(-11.1, 64.12) * mm, "radius": 6.6 * mm, "construction": true});
            skLineSegment(sketch, "E13.15.6", {"start": v(-6.46, 58.07) * mm, "end": v(-14.01, 57.08) * mm});
            skPoint(sketch, "E13.15.7", {"position": v(-5, 61.6) * mm});
            skPoint(sketch, "E13.center", {"position": v(0.68, 1.6) * mm});
            skCircle(sketch, "E14.cCircle", {"center": v(-39.96, 19.05) * mm, "radius": 6.6 * mm, "construction": true});
            skLineSegment(sketch, "E14.0", {"start": v(-33.36, 22.86) * mm, "end": v(-33.36, 15.24) * mm});
            skLineSegment(sketch, "E14.1", {"start": v(-33.36, 15.24) * mm, "end": v(-39.96, 11.43) * mm});
            skLineSegment(sketch, "E14.2", {"start": v(-39.96, 11.43) * mm, "end": v(-46.56, 15.24) * mm});
            skLineSegment(sketch, "E14.3", {"start": v(-46.56, 15.24) * mm, "end": v(-46.56, 22.86) * mm});
            skLineSegment(sketch, "E14.4", {"start": v(-46.56, 22.86) * mm, "end": v(-39.96, 26.67) * mm});
            skLineSegment(sketch, "E14.5", {"start": v(-39.96, 26.67) * mm, "end": v(-33.36, 22.86) * mm});
            skPoint(sketch, "E14.0.midPoint", {"position": v(-33.36, 19.05) * mm});
            skCircle(sketch, "E15", {"center": v(0.47, 0.22) * mm, "radius": 44.6 * mm, "construction": true});
            skLineSegment(sketch, "E16.1.0", {"start": v(-41.17, -4.9) * mm, "end": v(-48.73, -3.9) * mm});
            skLineSegment(sketch, "E16.1.1", {"start": v(-39.45, 8.2) * mm, "end": v(-36.54, 1.15) * mm});
            skLineSegment(sketch, "E16.1.2", {"start": v(-47, 9.19) * mm, "end": v(-39.45, 8.2) * mm});
            skLineSegment(sketch, "E16.1.3", {"start": v(-51.65, 3.14) * mm, "end": v(-47, 9.19) * mm});
            skLineSegment(sketch, "E16.1.4", {"start": v(-48.73, -3.9) * mm, "end": v(-51.65, 3.14) * mm});
            skCircle(sketch, "E16.1.5", {"center": v(-44.1, 2.15) * mm, "radius": 6.6 * mm, "construction": true});
            skLineSegment(sketch, "E16.1.6", {"start": v(-36.54, 1.15) * mm, "end": v(-41.17, -4.9) * mm});
            skPoint(sketch, "E16.1.7", {"position": v(-38, 4.67) * mm});
            skLineSegment(sketch, "E16.2.0", {"start": v(-36.05, -20.44) * mm, "end": v(-43.4, -22.41) * mm});
            skLineSegment(sketch, "E16.2.1", {"start": v(-39.46, -7.7) * mm, "end": v(-34.07, -13.08) * mm});
            skLineSegment(sketch, "E16.2.2", {"start": v(-46.82, -9.66) * mm, "end": v(-39.46, -7.7) * mm});
            skLineSegment(sketch, "E16.2.3", {"start": v(-48.8, -17.02) * mm, "end": v(-46.82, -9.66) * mm});
            skLineSegment(sketch, "E16.2.4", {"start": v(-43.4, -22.41) * mm, "end": v(-48.8, -17.02) * mm});
            skCircle(sketch, "E16.2.5", {"center": v(-41.43, -15.05) * mm, "radius": 6.6 * mm, "construction": true});
            skLineSegment(sketch, "E16.2.6", {"start": v(-34.07, -13.08) * mm, "end": v(-36.05, -20.44) * mm});
            skPoint(sketch, "E16.2.7", {"position": v(-36.77, -10.39) * mm});
            skLineSegment(sketch, "E16.3.0", {"start": v(-25.36, -32.84) * mm, "end": v(-31.4, -37.48) * mm});
            skLineSegment(sketch, "E16.3.1", {"start": v(-33.4, -22.37) * mm, "end": v(-26.35, -25.29) * mm});
            skLineSegment(sketch, "E16.3.2", {"start": v(-39.44, -27) * mm, "end": v(-33.4, -22.37) * mm});
            skLineSegment(sketch, "E16.3.3", {"start": v(-38.44, -34.56) * mm, "end": v(-39.44, -27) * mm});
            skLineSegment(sketch, "E16.3.4", {"start": v(-31.4, -37.48) * mm, "end": v(-38.44, -34.56) * mm});
            skCircle(sketch, "E16.3.5", {"center": v(-32.4, -29.92) * mm, "radius": 6.6 * mm, "construction": true});
            skLineSegment(sketch, "E16.3.6", {"start": v(-26.35, -25.29) * mm, "end": v(-25.36, -32.84) * mm});
            skPoint(sketch, "E16.3.7", {"position": v(-29.87, -23.83) * mm});
            skLineSegment(sketch, "E16.4.0", {"start": v(-10.74, -40.2) * mm, "end": v(-14.55, -46.8) * mm});
            skLineSegment(sketch, "E16.4.1", {"start": v(-22.17, -33.6) * mm, "end": v(-14.55, -33.6) * mm});
            skLineSegment(sketch, "E16.4.2", {"start": v(-25.98, -40.2) * mm, "end": v(-22.17, -33.6) * mm});
            skLineSegment(sketch, "E16.4.3", {"start": v(-22.17, -46.8) * mm, "end": v(-25.98, -40.2) * mm});
            skLineSegment(sketch, "E16.4.4", {"start": v(-14.55, -46.8) * mm, "end": v(-22.17, -46.8) * mm});
            skCircle(sketch, "E16.4.5", {"center": v(-18.36, -40.2) * mm, "radius": 6.6 * mm, "construction": true});
            skLineSegment(sketch, "E16.4.6", {"start": v(-14.55, -33.6) * mm, "end": v(-10.74, -40.2) * mm});
            skPoint(sketch, "E16.4.7", {"position": v(-18.36, -33.6) * mm});
            skLineSegment(sketch, "E16.5.0", {"start": v(5.59, -41.42) * mm, "end": v(4.6, -48.97) * mm});
            skLineSegment(sketch, "E16.5.1", {"start": v(-7.5, -39.7) * mm, "end": v(-0.46, -36.78) * mm});
            skLineSegment(sketch, "E16.5.2", {"start": v(-8.5, -47.25) * mm, "end": v(-7.5, -39.7) * mm});
            skLineSegment(sketch, "E16.5.3", {"start": v(-2.45, -51.89) * mm, "end": v(-8.5, -47.25) * mm});
            skLineSegment(sketch, "E16.5.4", {"start": v(4.6, -48.97) * mm, "end": v(-2.45, -51.89) * mm});
            skCircle(sketch, "E16.5.5", {"center": v(-1.45, -44.33) * mm, "radius": 6.6 * mm, "construction": true});
            skLineSegment(sketch, "E16.5.6", {"start": v(-0.46, -36.78) * mm, "end": v(5.59, -41.42) * mm});
            skPoint(sketch, "E16.5.7", {"position": v(-3.98, -38.24) * mm});
            skLineSegment(sketch, "E16.6.0", {"start": v(21.13, -36.3) * mm, "end": v(23.1, -43.65) * mm});
            skLineSegment(sketch, "E16.6.1", {"start": v(8.38, -39.7) * mm, "end": v(13.77, -34.32) * mm});
            skLineSegment(sketch, "E16.6.2", {"start": v(10.35, -47.07) * mm, "end": v(8.38, -39.7) * mm});
            skLineSegment(sketch, "E16.6.3", {"start": v(17.72, -49.04) * mm, "end": v(10.35, -47.07) * mm});
            skLineSegment(sketch, "E16.6.4", {"start": v(23.1, -43.65) * mm, "end": v(17.72, -49.04) * mm});
            skCircle(sketch, "E16.6.5", {"center": v(15.74, -41.68) * mm, "radius": 6.6 * mm, "construction": true});
            skLineSegment(sketch, "E16.6.6", {"start": v(13.77, -34.32) * mm, "end": v(21.13, -36.3) * mm});
            skPoint(sketch, "E16.6.7", {"position": v(11.08, -37.01) * mm});
            skLineSegment(sketch, "E16.7.0", {"start": v(33.53, -25.6) * mm, "end": v(38.17, -31.65) * mm});
            skLineSegment(sketch, "E16.7.1", {"start": v(23.06, -33.64) * mm, "end": v(25.98, -26.6) * mm});
            skLineSegment(sketch, "E16.7.2", {"start": v(27.7, -39.68) * mm, "end": v(23.06, -33.64) * mm});
            skLineSegment(sketch, "E16.7.3", {"start": v(35.25, -38.69) * mm, "end": v(27.7, -39.68) * mm});
            skLineSegment(sketch, "E16.7.4", {"start": v(38.17, -31.65) * mm, "end": v(35.25, -38.69) * mm});
            skCircle(sketch, "E16.7.5", {"center": v(30.62, -32.64) * mm, "radius": 6.6 * mm, "construction": true});
            skLineSegment(sketch, "E16.7.6", {"start": v(25.98, -26.6) * mm, "end": v(33.53, -25.6) * mm});
            skPoint(sketch, "E16.7.7", {"position": v(24.52, -30.12) * mm});
            skLineSegment(sketch, "E16.8.0", {"start": v(40.9, -10.98) * mm, "end": v(47.5, -14.8) * mm});
            skLineSegment(sketch, "E16.8.1", {"start": v(34.3, -22.41) * mm, "end": v(34.3, -14.8) * mm});
            skLineSegment(sketch, "E16.8.2", {"start": v(40.9, -26.22) * mm, "end": v(34.3, -22.41) * mm});
            skLineSegment(sketch, "E16.8.3", {"start": v(47.5, -22.41) * mm, "end": v(40.9, -26.22) * mm});
            skLineSegment(sketch, "E16.8.4", {"start": v(47.5, -14.8) * mm, "end": v(47.5, -22.41) * mm});
            skCircle(sketch, "E16.8.5", {"center": v(40.9, -18.6) * mm, "radius": 6.6 * mm, "construction": true});
            skLineSegment(sketch, "E16.8.6", {"start": v(34.3, -14.8) * mm, "end": v(40.9, -10.98) * mm});
            skPoint(sketch, "E16.8.7", {"position": v(34.3, -18.6) * mm});
            skLineSegment(sketch, "E16.9.0", {"start": v(42.1, 5.34) * mm, "end": v(49.66, 4.35) * mm});
            skLineSegment(sketch, "E16.9.1", {"start": v(40.39, -7.74) * mm, "end": v(37.47, -0.7) * mm});
            skLineSegment(sketch, "E16.9.2", {"start": v(47.94, -8.74) * mm, "end": v(40.39, -7.74) * mm});
            skLineSegment(sketch, "E16.9.3", {"start": v(52.58, -2.7) * mm, "end": v(47.94, -8.74) * mm});
            skLineSegment(sketch, "E16.9.4", {"start": v(49.66, 4.35) * mm, "end": v(52.58, -2.7) * mm});
            skCircle(sketch, "E16.9.5", {"center": v(45.03, -1.7) * mm, "radius": 6.6 * mm, "construction": true});
            skLineSegment(sketch, "E16.9.6", {"start": v(37.47, -0.7) * mm, "end": v(42.1, 5.34) * mm});
            skPoint(sketch, "E16.9.7", {"position": v(38.93, -4.22) * mm});
            skLineSegment(sketch, "E16.10.0", {"start": v(36.98, 20.89) * mm, "end": v(44.34, 22.86) * mm});
            skLineSegment(sketch, "E16.10.1", {"start": v(40.4, 8.14) * mm, "end": v(35, 13.53) * mm});
            skLineSegment(sketch, "E16.10.2", {"start": v(47.76, 10.11) * mm, "end": v(40.4, 8.14) * mm});
            skLineSegment(sketch, "E16.10.3", {"start": v(49.73, 17.47) * mm, "end": v(47.76, 10.11) * mm});
            skLineSegment(sketch, "E16.10.4", {"start": v(44.34, 22.86) * mm, "end": v(49.73, 17.47) * mm});
            skCircle(sketch, "E16.10.5", {"center": v(42.37, 15.5) * mm, "radius": 6.6 * mm, "construction": true});
            skLineSegment(sketch, "E16.10.6", {"start": v(35, 13.53) * mm, "end": v(36.98, 20.89) * mm});
            skPoint(sketch, "E16.10.7", {"position": v(37.7, 10.83) * mm});
            skLineSegment(sketch, "E16.11.0", {"start": v(26.3, 33.29) * mm, "end": v(32.34, 37.93) * mm});
            skLineSegment(sketch, "E16.11.1", {"start": v(34.33, 22.82) * mm, "end": v(27.29, 25.73) * mm});
            skLineSegment(sketch, "E16.11.2", {"start": v(40.37, 27.46) * mm, "end": v(34.33, 22.82) * mm});
            skLineSegment(sketch, "E16.11.3", {"start": v(39.38, 35.01) * mm, "end": v(40.37, 27.46) * mm});
            skLineSegment(sketch, "E16.11.4", {"start": v(32.34, 37.93) * mm, "end": v(39.38, 35.01) * mm});
            skCircle(sketch, "E16.11.5", {"center": v(33.33, 30.37) * mm, "radius": 6.6 * mm, "construction": true});
            skLineSegment(sketch, "E16.11.6", {"start": v(27.29, 25.73) * mm, "end": v(26.3, 33.29) * mm});
            skPoint(sketch, "E16.11.7", {"position": v(30.8, 24.27) * mm});
            skLineSegment(sketch, "E16.12.0", {"start": v(11.67, 40.65) * mm, "end": v(15.48, 47.25) * mm});
            skLineSegment(sketch, "E16.12.1", {"start": v(23.1, 34.06) * mm, "end": v(15.48, 34.06) * mm});
            skLineSegment(sketch, "E16.12.2", {"start": v(26.91, 40.65) * mm, "end": v(23.1, 34.06) * mm});
            skLineSegment(sketch, "E16.12.3", {"start": v(23.1, 47.25) * mm, "end": v(26.91, 40.65) * mm});
            skLineSegment(sketch, "E16.12.4", {"start": v(15.48, 47.25) * mm, "end": v(23.1, 47.25) * mm});
            skCircle(sketch, "E16.12.5", {"center": v(19.3, 40.65) * mm, "radius": 6.6 * mm, "construction": true});
            skLineSegment(sketch, "E16.12.6", {"start": v(15.48, 34.06) * mm, "end": v(11.67, 40.65) * mm});
            skPoint(sketch, "E16.12.7", {"position": v(19.3, 34.06) * mm});
            skLineSegment(sketch, "E16.13.0", {"start": v(-4.65, 41.87) * mm, "end": v(-3.66, 49.42) * mm});
            skLineSegment(sketch, "E16.13.1", {"start": v(8.43, 40.14) * mm, "end": v(1.4, 37.23) * mm});
            skLineSegment(sketch, "E16.13.2", {"start": v(9.43, 47.7) * mm, "end": v(8.43, 40.14) * mm});
            skLineSegment(sketch, "E16.13.3", {"start": v(3.38, 52.34) * mm, "end": v(9.43, 47.7) * mm});
            skLineSegment(sketch, "E16.13.4", {"start": v(-3.66, 49.42) * mm, "end": v(3.38, 52.34) * mm});
            skCircle(sketch, "E16.13.5", {"center": v(2.39, 44.78) * mm, "radius": 6.6 * mm, "construction": true});
            skLineSegment(sketch, "E16.13.6", {"start": v(1.4, 37.23) * mm, "end": v(-4.65, 41.87) * mm});
            skPoint(sketch, "E16.13.7", {"position": v(4.91, 38.68) * mm});
            skLineSegment(sketch, "E16.14.0", {"start": v(-20.2, 36.74) * mm, "end": v(-22.17, 44.1) * mm});
            skLineSegment(sketch, "E16.14.1", {"start": v(-7.45, 40.15) * mm, "end": v(-12.84, 34.77) * mm});
            skLineSegment(sketch, "E16.14.2", {"start": v(-9.42, 47.51) * mm, "end": v(-7.45, 40.15) * mm});
            skLineSegment(sketch, "E16.14.3", {"start": v(-16.78, 49.49) * mm, "end": v(-9.42, 47.51) * mm});
            skLineSegment(sketch, "E16.14.4", {"start": v(-22.17, 44.1) * mm, "end": v(-16.78, 49.49) * mm});
            skCircle(sketch, "E16.14.5", {"center": v(-14.8, 42.13) * mm, "radius": 6.6 * mm, "construction": true});
            skLineSegment(sketch, "E16.14.6", {"start": v(-12.84, 34.77) * mm, "end": v(-20.2, 36.74) * mm});
            skPoint(sketch, "E16.14.7", {"position": v(-10.14, 37.46) * mm});
            skLineSegment(sketch, "E16.15.0", {"start": v(-32.6, 26.05) * mm, "end": v(-37.24, 32.1) * mm});
            skLineSegment(sketch, "E16.15.1", {"start": v(-22.13, 34.08) * mm, "end": v(-25.04, 27.04) * mm});
            skLineSegment(sketch, "E16.15.2", {"start": v(-26.76, 40.13) * mm, "end": v(-22.13, 34.08) * mm});
            skLineSegment(sketch, "E16.15.3", {"start": v(-34.32, 39.14) * mm, "end": v(-26.76, 40.13) * mm});
            skLineSegment(sketch, "E16.15.4", {"start": v(-37.24, 32.1) * mm, "end": v(-34.32, 39.14) * mm});
            skCircle(sketch, "E16.15.5", {"center": v(-29.68, 33.1) * mm, "radius": 6.6 * mm, "construction": true});
            skLineSegment(sketch, "E16.15.6", {"start": v(-25.04, 27.04) * mm, "end": v(-32.6, 26.05) * mm});
            skPoint(sketch, "E16.15.7", {"position": v(-23.58, 30.56) * mm});
            skCircle(sketch, "E17", {"center": v(0, 0) * mm, "radius": 26.1 * mm});
            skLineSegment(sketch, "E18.2.16.0", {"start": v(52.77, 75.62) * mm, "end": v(54.36, 83.08) * mm});
            skLineSegment(sketch, "E18.3.16.0", {"start": v(65.68, 72.88) * mm, "end": v(58.44, 70.52) * mm});
            skLineSegment(sketch, "E18.6.16.0", {"start": v(67.27, 80.33) * mm, "end": v(65.68, 72.88) * mm});
            skLineSegment(sketch, "E18.9.16.0", {"start": v(61.6, 85.43) * mm, "end": v(67.27, 80.33) * mm});
            skLineSegment(sketch, "E18.12.16.0", {"start": v(54.36, 83.08) * mm, "end": v(61.6, 85.43) * mm});
            skCircle(sketch, "E18.15.16.0", {"center": v(60.02, 77.98) * mm, "radius": 6.6 * mm, "construction": true});
            skLineSegment(sketch, "E18.17.16.0", {"start": v(58.44, 70.52) * mm, "end": v(52.77, 75.62) * mm});
            skPoint(sketch, "E18.20.16.0", {"position": v(62.06, 71.7) * mm});
            skLineSegment(sketch, "E18.2.17.0", {"start": v(26.91, 88.1) * mm, "end": v(26.12, 95.67) * mm});
            skLineSegment(sketch, "E18.3.17.0", {"start": v(40.04, 89.47) * mm, "end": v(33.88, 85) * mm});
            skLineSegment(sketch, "E18.6.17.0", {"start": v(39.24, 97.05) * mm, "end": v(40.04, 89.47) * mm});
            skLineSegment(sketch, "E18.9.17.0", {"start": v(32.28, 100.15) * mm, "end": v(39.24, 97.05) * mm});
            skLineSegment(sketch, "E18.12.17.0", {"start": v(26.12, 95.67) * mm, "end": v(32.28, 100.15) * mm});
            skCircle(sketch, "E18.15.17.0", {"center": v(33.08, 92.57) * mm, "radius": 6.6 * mm, "construction": true});
            skLineSegment(sketch, "E18.17.17.0", {"start": v(33.88, 85) * mm, "end": v(26.91, 88.1) * mm});
            skPoint(sketch, "E18.20.17.0", {"position": v(36.96, 87.24) * mm});
            skLineSegment(sketch, "E18.2.18.0", {"start": v(-1.53, 91.97) * mm, "end": v(-4.63, 98.93) * mm});
            skLineSegment(sketch, "E18.3.18.0", {"start": v(10.52, 97.34) * mm, "end": v(6.04, 91.17) * mm});
            skLineSegment(sketch, "E18.6.18.0", {"start": v(7.42, 104.3) * mm, "end": v(10.52, 97.34) * mm});
            skLineSegment(sketch, "E18.9.18.0", {"start": v(-0.15, 105.1) * mm, "end": v(7.42, 104.3) * mm});
            skLineSegment(sketch, "E18.12.18.0", {"start": v(-4.63, 98.93) * mm, "end": v(-0.15, 105.1) * mm});
            skCircle(sketch, "E18.15.18.0", {"center": v(2.95, 98.13) * mm, "radius": 6.6 * mm, "construction": true});
            skLineSegment(sketch, "E18.17.18.0", {"start": v(6.04, 91.17) * mm, "end": v(-1.53, 91.97) * mm});
            skPoint(sketch, "E18.20.18.0", {"position": v(8.28, 94.25) * mm});
            skLineSegment(sketch, "E18.2.19.0", {"start": v(-29.79, 86.86) * mm, "end": v(-34.88, 92.52) * mm});
            skLineSegment(sketch, "E18.3.19.0", {"start": v(-19.98, 95.7) * mm, "end": v(-22.33, 88.44) * mm});
            skLineSegment(sketch, "E18.6.19.0", {"start": v(-25.08, 101.35) * mm, "end": v(-19.98, 95.7) * mm});
            skLineSegment(sketch, "E18.9.19.0", {"start": v(-32.53, 99.77) * mm, "end": v(-25.08, 101.35) * mm});
            skLineSegment(sketch, "E18.12.19.0", {"start": v(-34.88, 92.52) * mm, "end": v(-32.53, 99.77) * mm});
            skCircle(sketch, "E18.15.19.0", {"center": v(-27.43, 94.1) * mm, "radius": 6.6 * mm, "construction": true});
            skLineSegment(sketch, "E18.17.19.0", {"start": v(-22.33, 88.44) * mm, "end": v(-29.79, 86.86) * mm});
            skPoint(sketch, "E18.20.19.0", {"position": v(-21.16, 92.07) * mm});
            skSolve(sketch);
        }
        {
            var Q0;
            Q0 = qSketchRegion(id + "F4", true);
            extrude(context, id + "F5", {"entities" : qUnion([Q0]), "operationType" : NewBodyOperationType.REMOVE, "oppositeDirection" : true, "depth" : 25.4 * mm, "offsetDistance" : 25.4 * mm});
        }
    });
